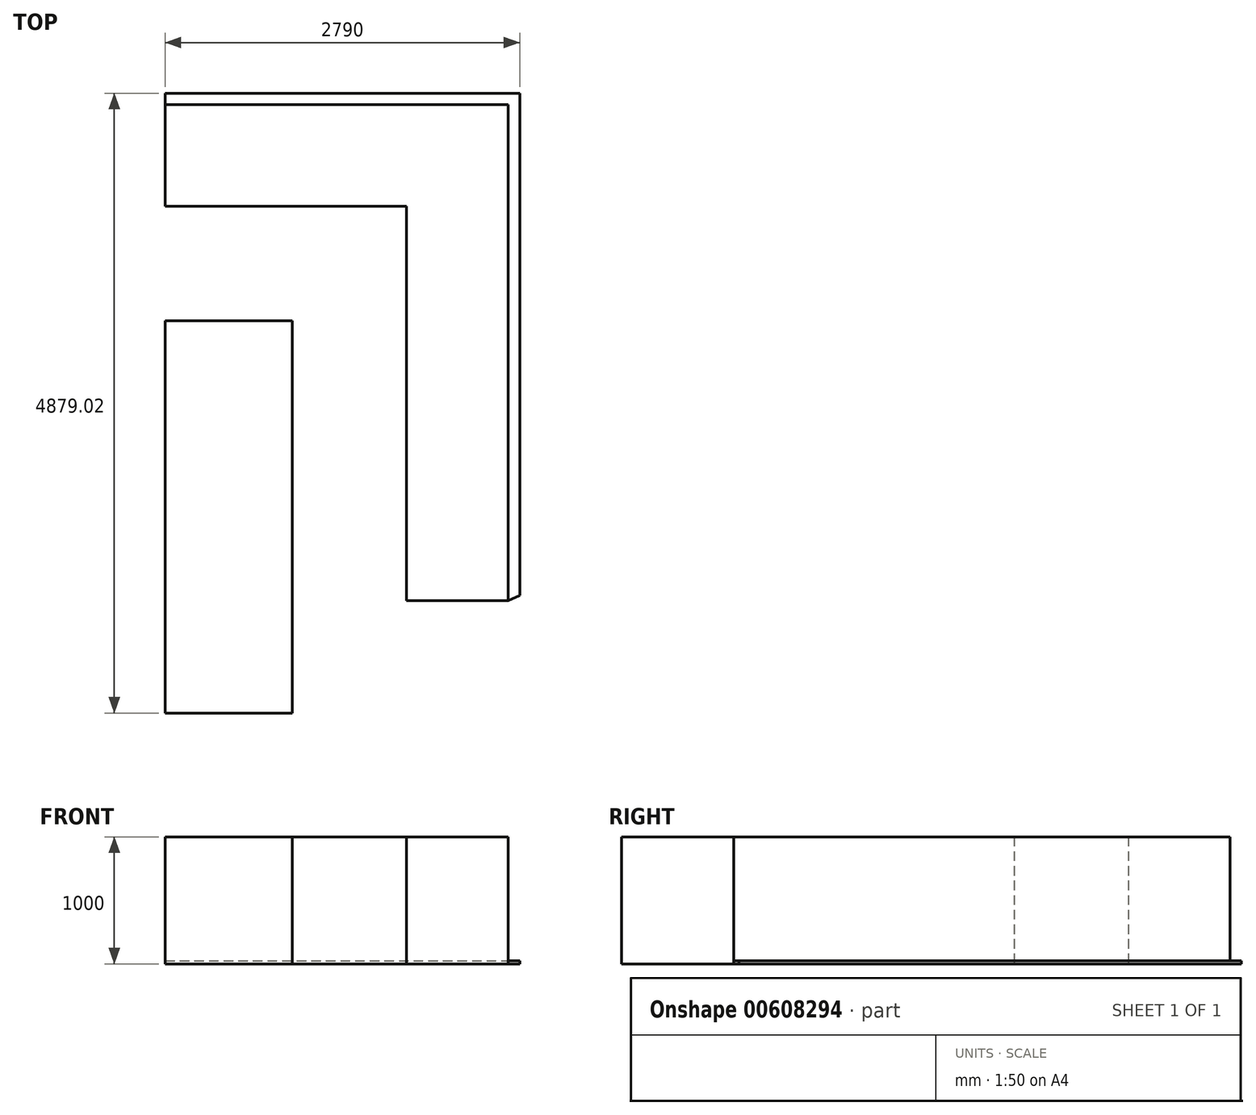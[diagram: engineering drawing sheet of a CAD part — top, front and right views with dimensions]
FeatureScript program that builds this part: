
annotation { "Feature Type Name" : "Feature", "Feature Type Description" : "" }
export const myFeature = defineFeature(function(context is Context, id is Id, definition is map)
    precondition{}
    {
        {
            var Q0;
            Q0=qCreatedBy(makeId("Top.planeOp"),FACE);
            var sketch = newSketch(context, id + "F0", { "sketchPlane" : qUnion([Q0])});
            skLineSegment(sketch, "E0", {"start": v(-1722.32, 127.3) * mm, "end": v(977.68, 127.3) * mm});
            skLineSegment(sketch, "E1", {"start": v(977.68, 127.3) * mm, "end": v(2842.91, -3872.7) * mm});
            skLineSegment(sketch, "E2", {"start": v(2842.91, -3872.7) * mm, "end": v(1150.83, -4661.73) * mm});
            skLineSegment(sketch, "E3", {"start": v(977.68, 127.3) * mm, "end": v(977.68, -3778.55) * mm});
            skLineSegment(sketch, "E4", {"start": v(-1722.32, 127.3) * mm, "end": v(-1722.32, -672.7) * mm});
            skLineSegment(sketch, "E5", {"start": v(-1722.32, -672.7) * mm, "end": v(177.68, -672.7) * mm});
            skLineSegment(sketch, "E6", {"start": v(177.68, -672.7) * mm, "end": v(177.68, -3778.55) * mm});
            skLineSegment(sketch, "E7", {"start": v(177.68, -3778.55) * mm, "end": v(977.68, -3778.55) * mm});
            skLineSegment(sketch, "E8", {"start": v(977.68, -3778.55) * mm, "end": v(1445.36, -3560.47) * mm});
            skLineSegment(sketch, "E9", {"start": v(1445.36, -3560.47) * mm, "end": v(1445.36, -875.64) * mm});
            skLineSegment(sketch, "E10", {"start": v(-1722.32, -1572.7) * mm, "end": v(-722.32, -1572.7) * mm});
            skLineSegment(sketch, "E11", {"start": v(-722.32, -1572.7) * mm, "end": v(-722.32, -3778.55) * mm});
            skLineSegment(sketch, "E12", {"start": v(-1722.32, -3778.55) * mm, "end": v(-1722.32, -1572.7) * mm});
            skLineSegment(sketch, "E13", {"start": v(-722.32, -4661.73) * mm, "end": v(-1722.32, -4661.73) * mm});
            skLineSegment(sketch, "E14", {"start": v(-1722.32, -3778.55) * mm, "end": v(-1722.32, -4661.73) * mm});
            skLineSegment(sketch, "E15", {"start": v(-1722.32, -4661.73) * mm, "end": v(-722.32, -4661.73) * mm});
            skLineSegment(sketch, "E16", {"start": v(-722.32, -4661.73) * mm, "end": v(-722.32, -3778.55) * mm});
            skLineSegment(sketch, "E17", {"start": v(977.68, -3778.55) * mm, "end": v(1067.68, -3778.55) * mm});
            skLineSegment(sketch, "E18", {"start": v(1067.68, -3778.55) * mm, "end": v(1067.68, -65.71) * mm});
            skLineSegment(sketch, "E19", {"start": v(-1722.32, 127.3) * mm, "end": v(-1722.32, 217.3) * mm});
            skLineSegment(sketch, "E20", {"start": v(-1722.32, 217.3) * mm, "end": v(1067.68, 217.3) * mm});
            skLineSegment(sketch, "E21", {"start": v(1067.68, 217.3) * mm, "end": v(1067.68, -65.71) * mm});
            skSolve(sketch);
        }
        {
            var Q0;
            Q0=makeQuery(id+"F0.imprint","IMPRINT",FACE,{"disambiguationData":[TD([[makeQuery(id+"F0.imprint","IMPRINT",EDGE,{"derivedFrom":sQuery(id+"F0.wireOp",EDGE,"E10")}),-1.0]])]});
            extrude(context, id + "F1", {"entities" : qUnion([Q0]), "depth" : 1000 * mm, "offsetDistance" : 25 * mm});
        }
        {
            var Q0;
            Q0=makeQuery(id+"F0.imprint","IMPRINT",FACE,{"disambiguationData":[TD([[makeQuery(id+"F0.imprint","IMPRINT",EDGE,{"derivedFrom":sQuery(id+"F0.wireOp",EDGE,"E0")}),-1.0]])]});
            extrude(context, id + "F2", {"entities" : qUnion([Q0]), "depth" : 1000 * mm, "offsetDistance" : 25 * mm});
        }
        {
            var Q0;
            {var subQ1=sQuery(id+"F0.wireOp",EDGE,"E0");Q0=makeQuery(id+"F0.imprint","IMPRINT",FACE,{"disambiguationData":[TD([[makeQuery(id+"F0.imprint","IMPRINT",EDGE,{"derivedFrom":subQ1}),1.0]])]});}
            var Q1;
            {var subQ0=sQuery(id+"F0.wireOp",EDGE,"E3");Q1=makeQuery(id+"F0.imprint","IMPRINT",FACE,{"disambiguationData":[TD([[makeQuery(id+"F0.imprint","IMPRINT",EDGE,{"derivedFrom":subQ0}),1.0]])]});}
            extrude(context, id + "F3", {"entities" : qUnion([Q0, Q1]), "operationType" : NewBodyOperationType.ADD, "depth" : 25 * mm, "offsetDistance" : 25 * mm});
        }
    });
